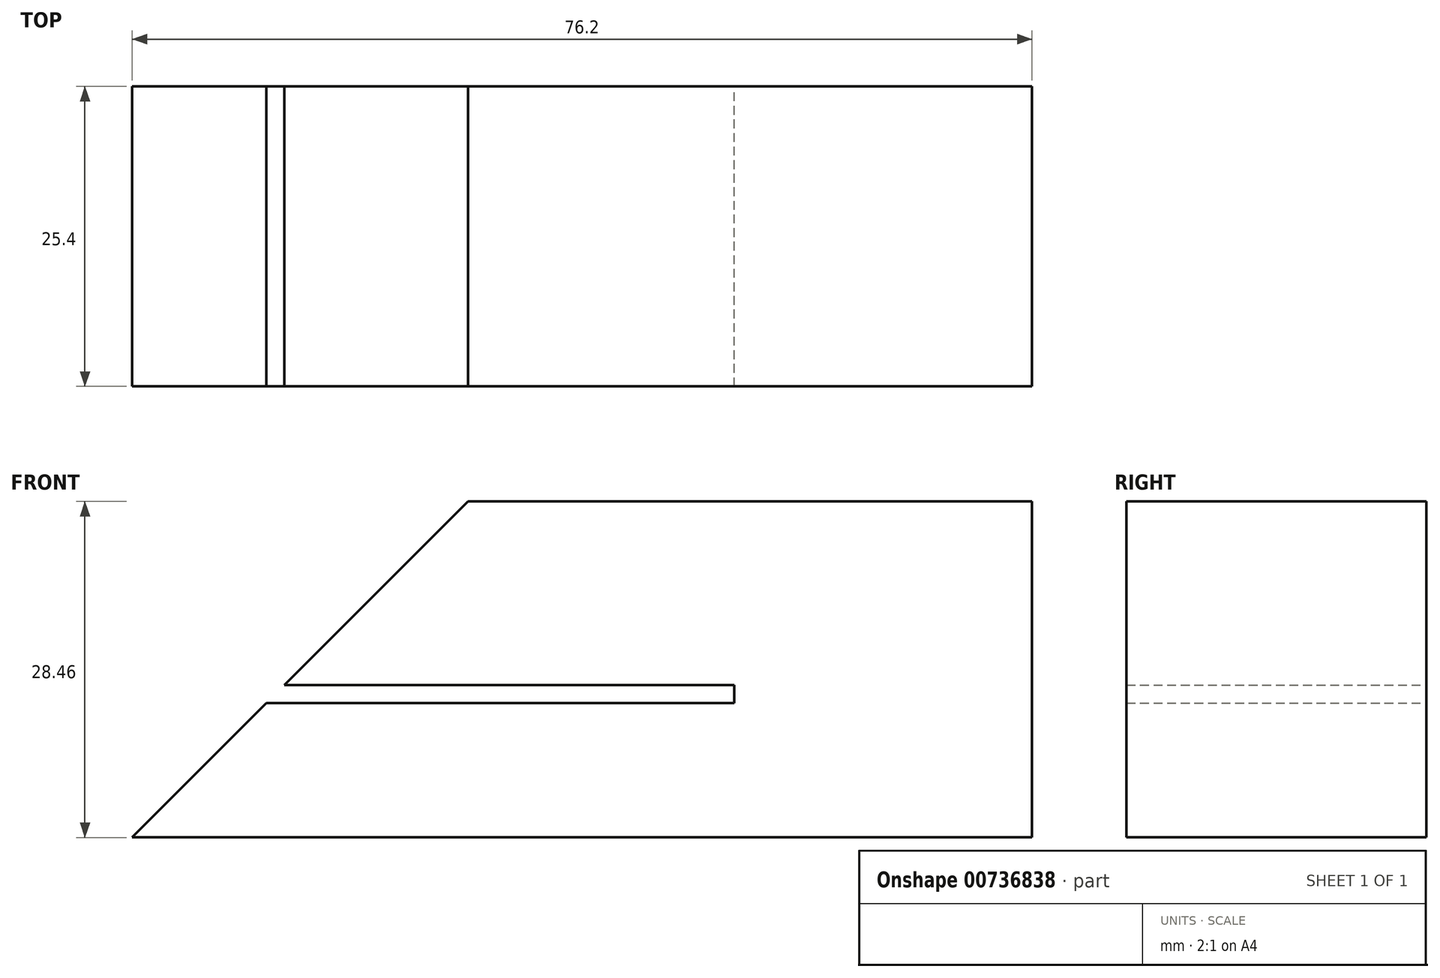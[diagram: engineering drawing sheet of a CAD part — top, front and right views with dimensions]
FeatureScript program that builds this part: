
annotation { "Feature Type Name" : "Feature", "Feature Type Description" : "" }
export const myFeature = defineFeature(function(context is Context, id is Id, definition is map)
    precondition{}
    {
        {
            var Q0;
            Q0=qCreatedBy(makeId("Front.planeOp"),FACE);
            var sketch = newSketch(context, id + "F0", { "sketchPlane" : qUnion([Q0])});
            skLineSegment(sketch, "E0.top", {"start": v(-54.85, -18.54) * mm, "end": v(21.35, -18.54) * mm});
            skLineSegment(sketch, "E1", {"start": v(-54.85, -18.54) * mm, "end": v(-43.48, -7.16) * mm});
            skLineSegment(sketch, "E2.bottom", {"start": v(-41.96, -5.64) * mm, "end": v(-3.86, -5.64) * mm});
            skLineSegment(sketch, "E2.top", {"start": v(-41.96, -7.16) * mm, "end": v(-3.86, -7.16) * mm});
            skLineSegment(sketch, "E2.right", {"start": v(-3.86, -5.64) * mm, "end": v(-3.86, -7.16) * mm});
            skLineSegment(sketch, "E3", {"start": v(-41.96, -7.16) * mm, "end": v(-43.48, -7.16) * mm});
            skLineSegment(sketch, "E4.trimOffspring", {"start": v(-41.96, -5.64) * mm, "end": v(-26.4, 9.92) * mm});
            skLineSegment(sketch, "E5", {"start": v(21.35, 9.92) * mm, "end": v(-26.4, 9.92) * mm});
            skPoint(sketch, "E6.orphan", {"position": v(21.35, 57.66) * mm});
            skLineSegment(sketch, "E7.trimOffspring", {"start": v(21.35, 9.92) * mm, "end": v(21.35, -18.54) * mm});
            skPoint(sketch, "E0.right.end.orphan", {"position": v(21.35, 19.56) * mm});
            skSolve(sketch);
        }
        {
            var Q0;
            Q0=makeQuery(id+"F0.imprint","IMPRINT",FACE,{"disambiguationData":[TD([[makeQuery(id+"F0.imprint","IMPRINT",EDGE,{"derivedFrom":sQuery(id+"F0.wireOp",EDGE,"E0.top")}),1.0]])]});
            extrude(context, id + "F1", {"entities" : qUnion([Q0]), "depth" : 25.4 * mm, "offsetDistance" : 25.4 * mm});
        }
    });
